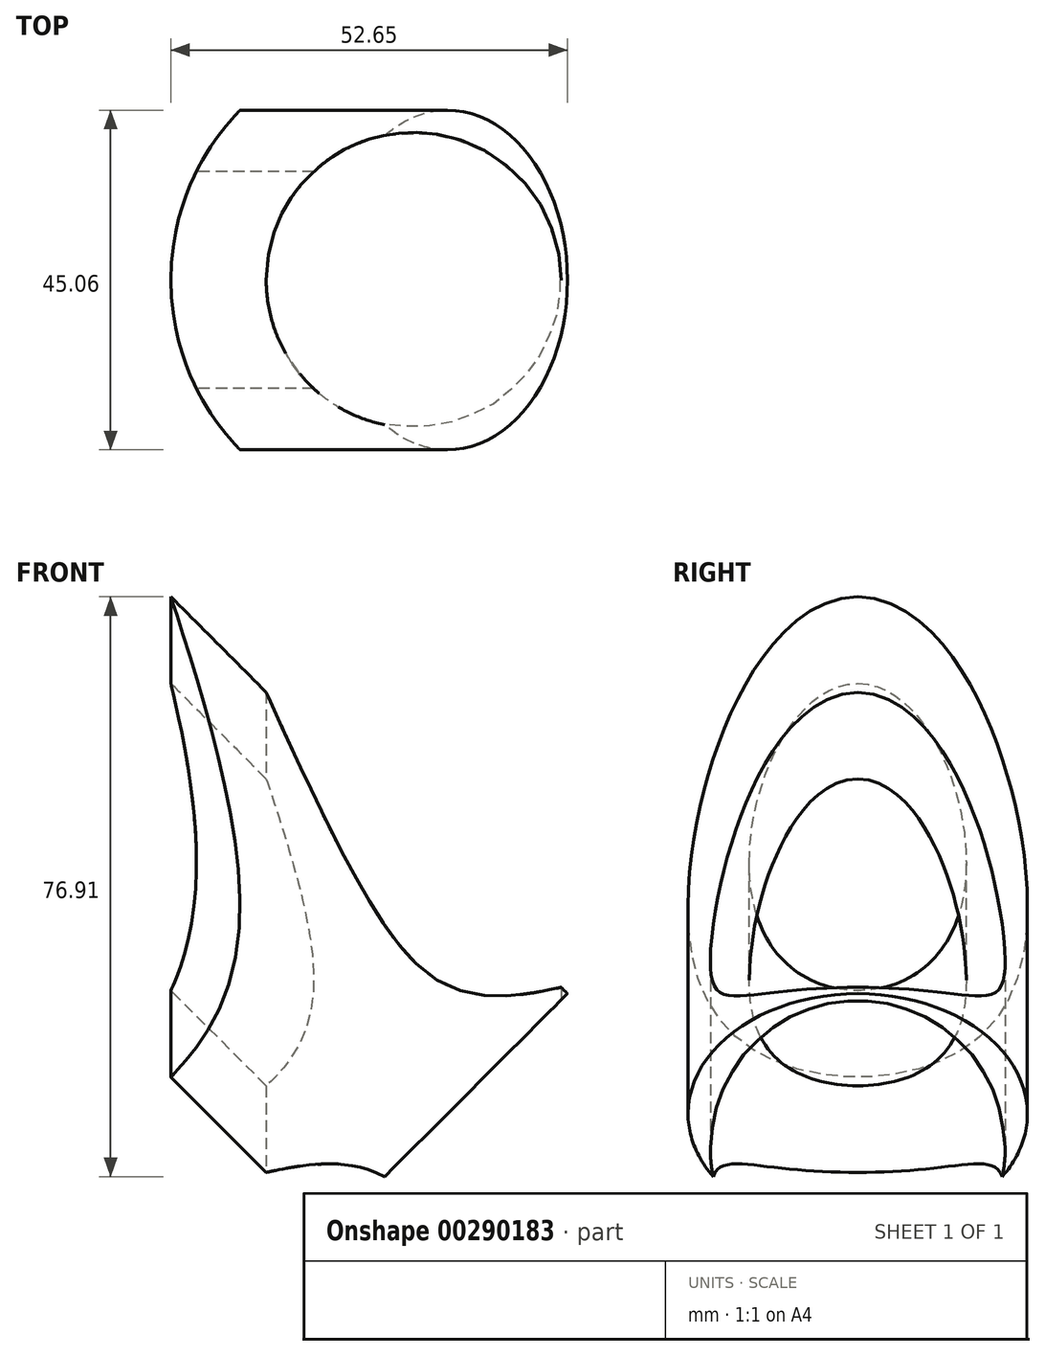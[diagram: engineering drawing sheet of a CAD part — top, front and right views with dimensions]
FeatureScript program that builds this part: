
annotation { "Feature Type Name" : "Feature", "Feature Type Description" : "" }
export const myFeature = defineFeature(function(context is Context, id is Id, definition is map)
    precondition{}
    {
        {
            var Q0;
            Q0=qCreatedBy(makeId("Top.planeOp"),FACE);
            var sketch = newSketch(context, id + "F0", { "sketchPlane" : qUnion([Q0])});
            skCircle(sketch, "E0", {"center": v(0, 0) * mm, "radius": 32.23 * mm});
            skCircle(sketch, "E1", {"center": v(0, 0) * mm, "radius": 19.57 * mm});
            skLineSegment(sketch, "E2", {"start": v(0, 32.23) * mm, "end": v(0, -32.23) * mm, "construction": true});
            skSolve(sketch);
        }
        {
            var Q0;
            Q0=qSketchRegion(id+"F0",true);
            extrude(context, id + "F1", {"entities" : qUnion([Q0]), "depth" : 254 * mm, "hasSecondDirection" : true, "secondDirectionOppositeDirection" : true, "secondDirectionDepth" : 254 * mm});
        }
        {
            var Q0;
            Q0=sQuery(id+"F0.wireOp",EDGE,"E2");
            cPlane(context, id + "F2", {"entities" : qUnion([Q0]), "cplaneType" : CPlaneType.LINE_ANGLE, "offset" : 25.4 * mm, "angle" : 45 * degree, "width" : 152.4 * mm, "height" : 152.4 * mm});
        }
        {
            var Q0;
            Q0=qCreatedBy(id+"F2.planeOp",FACE);
            cPlane(context, id + "F3", {"entities" : qUnion([Q0]), "cplaneType" : CPlaneType.OFFSET, "offset" : 127 * mm, "oppositeDirection" : true, "width" : 152.4 * mm, "height" : 152.4 * mm});
        }
        {
            var Q0;
            Q0=qCreatedBy(id+"F3.planeOp",FACE);
            var sketch = newSketch(context, id + "F4", { "sketchPlane" : qUnion([Q0])});
            skCircle(sketch, "E3", {"center": v(0, 0) * mm, "radius": 14.4 * mm});
            skCircle(sketch, "E4", {"center": v(0, 0) * mm, "radius": 22.52 * mm});
            skSolve(sketch);
        }
        {
            var Q0;
            Q0=qSketchRegion(id+"F4",true);
            extrude(context, id + "F5", {"entities" : qUnion([Q0]), "depth" : 133.35 * mm, "hasSecondDirection" : true, "secondDirectionOppositeDirection" : true, "secondDirectionDepth" : 127 * mm});
        }
        {
            var Q0;
            Q0=makeQuery(id+"F1.opExtrude","SWEPT_BODY",BODY,{"disambiguationData":[OSD([sQuery(id+"F0.wireOp",EDGE,"E0"),sQuery(id+"F0.wireOp",EDGE,"E1")])]});
            var Q1;
            Q1=makeQuery(id+"F5.opExtrude","SWEPT_BODY",BODY,{"disambiguationData":[OSD([sQuery(id+"F4.wireOp",EDGE,"E3"),sQuery(id+"F4.wireOp",EDGE,"E4")])]});
            booleanBodies(context, id + "F6", {"operationType" : BooleanOperationType.INTERSECTION, "tools" : qUnion([Q0, Q1]), "keepTools" : true});
        }
        {
            var Q0;
            Q0=makeQuery(id+"F6.opBoolean","INTERSECT",BODY,{"derivedFrom":[makeQuery(id+"F1.opExtrude","SWEPT_BODY",BODY,{"disambiguationData":[OSD([sQuery(id+"F0.wireOp",EDGE,"E0"),sQuery(id+"F0.wireOp",EDGE,"E1")])]}),makeQuery(id+"F5.opExtrude","SWEPT_BODY",BODY,{"disambiguationData":[OSD([sQuery(id+"F4.wireOp",EDGE,"E3"),sQuery(id+"F4.wireOp",EDGE,"E4")])]})]});
            var Q1;
            Q1=makeQuery(id+"F1.opExtrude","SWEPT_BODY",BODY,{"disambiguationData":[OSD([sQuery(id+"F0.wireOp",EDGE,"E0"),sQuery(id+"F0.wireOp",EDGE,"E1")])]});
            booleanBodies(context, id + "F7", {"operationType" : BooleanOperationType.INTERSECTION, "tools" : qUnion([Q0, Q1]), "keepTools" : true});
        }
        {
            var Q0;
            Q0=makeQuery(id+"F6.opBoolean","INTERSECT",BODY,{"derivedFrom":[makeQuery(id+"F1.opExtrude","SWEPT_BODY",BODY,{"disambiguationData":[OSD([sQuery(id+"F0.wireOp",EDGE,"E0"),sQuery(id+"F0.wireOp",EDGE,"E1")])]}),makeQuery(id+"F5.opExtrude","SWEPT_BODY",BODY,{"disambiguationData":[OSD([sQuery(id+"F4.wireOp",EDGE,"E3"),sQuery(id+"F4.wireOp",EDGE,"E4")])]})]});
            var Q1;
            Q1=makeQuery(id+"F5.opExtrude","SWEPT_BODY",BODY,{"disambiguationData":[OSD([sQuery(id+"F4.wireOp",EDGE,"E3"),sQuery(id+"F4.wireOp",EDGE,"E4")])]});
            var Q2;
            Q2=makeQuery(id+"F1.opExtrude","SWEPT_BODY",BODY,{"disambiguationData":[OSD([sQuery(id+"F0.wireOp",EDGE,"E0"),sQuery(id+"F0.wireOp",EDGE,"E1")])]});
            booleanBodies(context, id + "F8", {"operationType" : BooleanOperationType.SUBTRACTION, "tools" : qUnion([Q0]), "targets" : qUnion([Q1, Q2])});
        }
        {
            var Q0;
            Q0=makeQuery(id+"F8.opBoolean","SPLIT",BODY,{"disambiguationData":[OD(0.0)],"derivedFrom":makeQuery(id+"F1.opExtrude","SWEPT_BODY",BODY,{"disambiguationData":[OSD([sQuery(id+"F0.wireOp",EDGE,"E0"),sQuery(id+"F0.wireOp",EDGE,"E1")])]})});
            var Q1;
            Q1=makeQuery(id+"F8.opBoolean","SPLIT",BODY,{"disambiguationData":[OD(1.0)],"derivedFrom":makeQuery(id+"F5.opExtrude","SWEPT_BODY",BODY,{"disambiguationData":[OSD([sQuery(id+"F4.wireOp",EDGE,"E3"),sQuery(id+"F4.wireOp",EDGE,"E4")])]})});
            deleteBodies(context, id + "F9", {"entities" : qUnion([Q0, Q1])});
        }
    });
